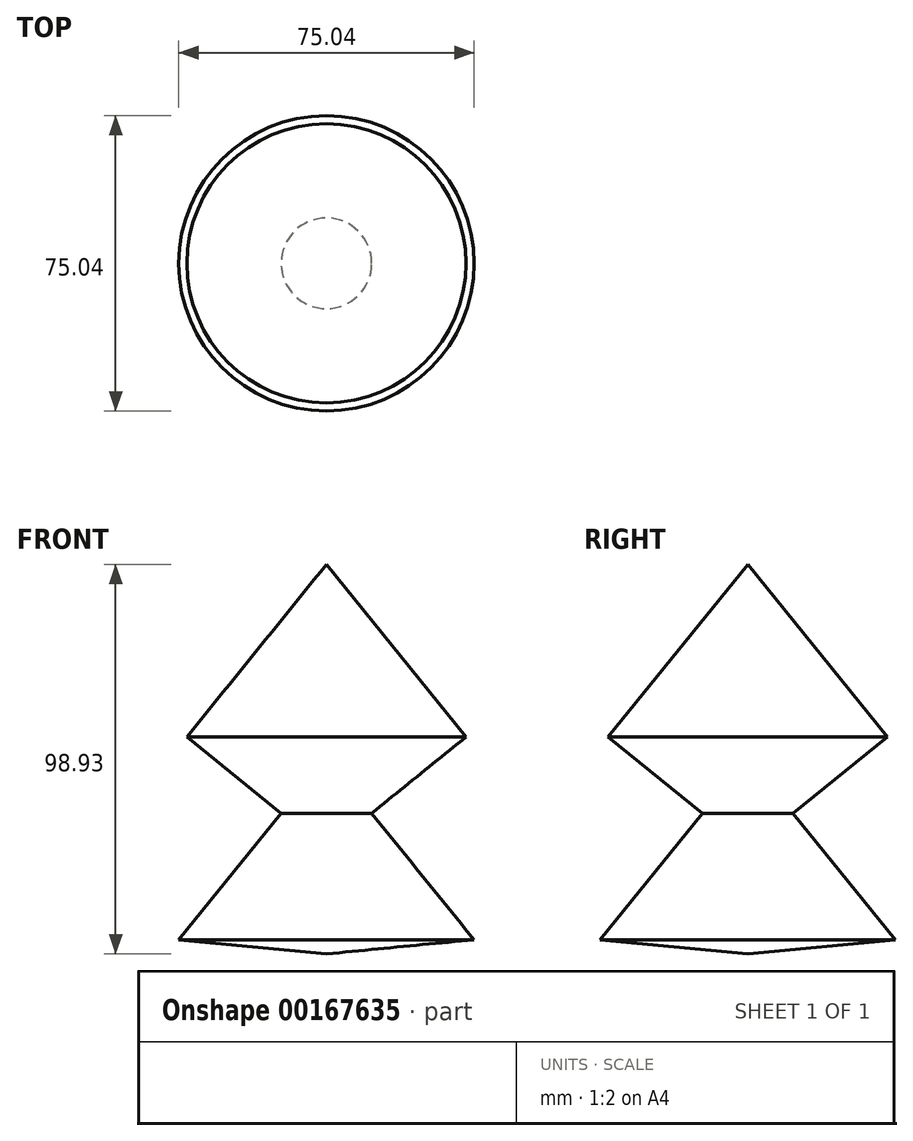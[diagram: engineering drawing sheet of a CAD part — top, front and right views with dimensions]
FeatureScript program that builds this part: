
annotation { "Feature Type Name" : "Feature", "Feature Type Description" : "" }
export const myFeature = defineFeature(function(context is Context, id is Id, definition is map)
    precondition{}
    {
        {
            var Q0;
            Q0=qCreatedBy(makeId("Front.planeOp"),FACE);
            var sketch = newSketch(context, id + "F0", { "sketchPlane" : qUnion([Q0])});
            skLineSegment(sketch, "E0", {"start": v(-48.72, 56.47) * mm, "end": v(-48.72, -42.46) * mm});
            skLineSegment(sketch, "E1", {"start": v(-48.72, 56.47) * mm, "end": v(-13.26, 12.66) * mm});
            skLineSegment(sketch, "E2", {"start": v(-13.26, 12.66) * mm, "end": v(-37.21, -6.72) * mm});
            skLineSegment(sketch, "E3", {"start": v(-37.21, -6.72) * mm, "end": v(-11.2, -38.85) * mm});
            skLineSegment(sketch, "E4", {"start": v(-11.2, -38.85) * mm, "end": v(-48.72, -42.46) * mm});
            skSolve(sketch);
        }
        {
            var Q0;
            Q0=makeQuery(id+"F0.imprint","IMPRINT",FACE,{"disambiguationData":[TD([[makeQuery(id+"F0.imprint","IMPRINT",EDGE,{"derivedFrom":sQuery(id+"F0.wireOp",EDGE,"E0")}),1.0]])]});
            var Q1;
            Q1=sQuery(id+"F0.wireOp",EDGE,"E0");
            revolve(context, id + "F1", {"entities" : qUnion([Q0]), "axis" : qUnion([Q1]), "revolveType" : RevolveType.FULL});
        }
    });
